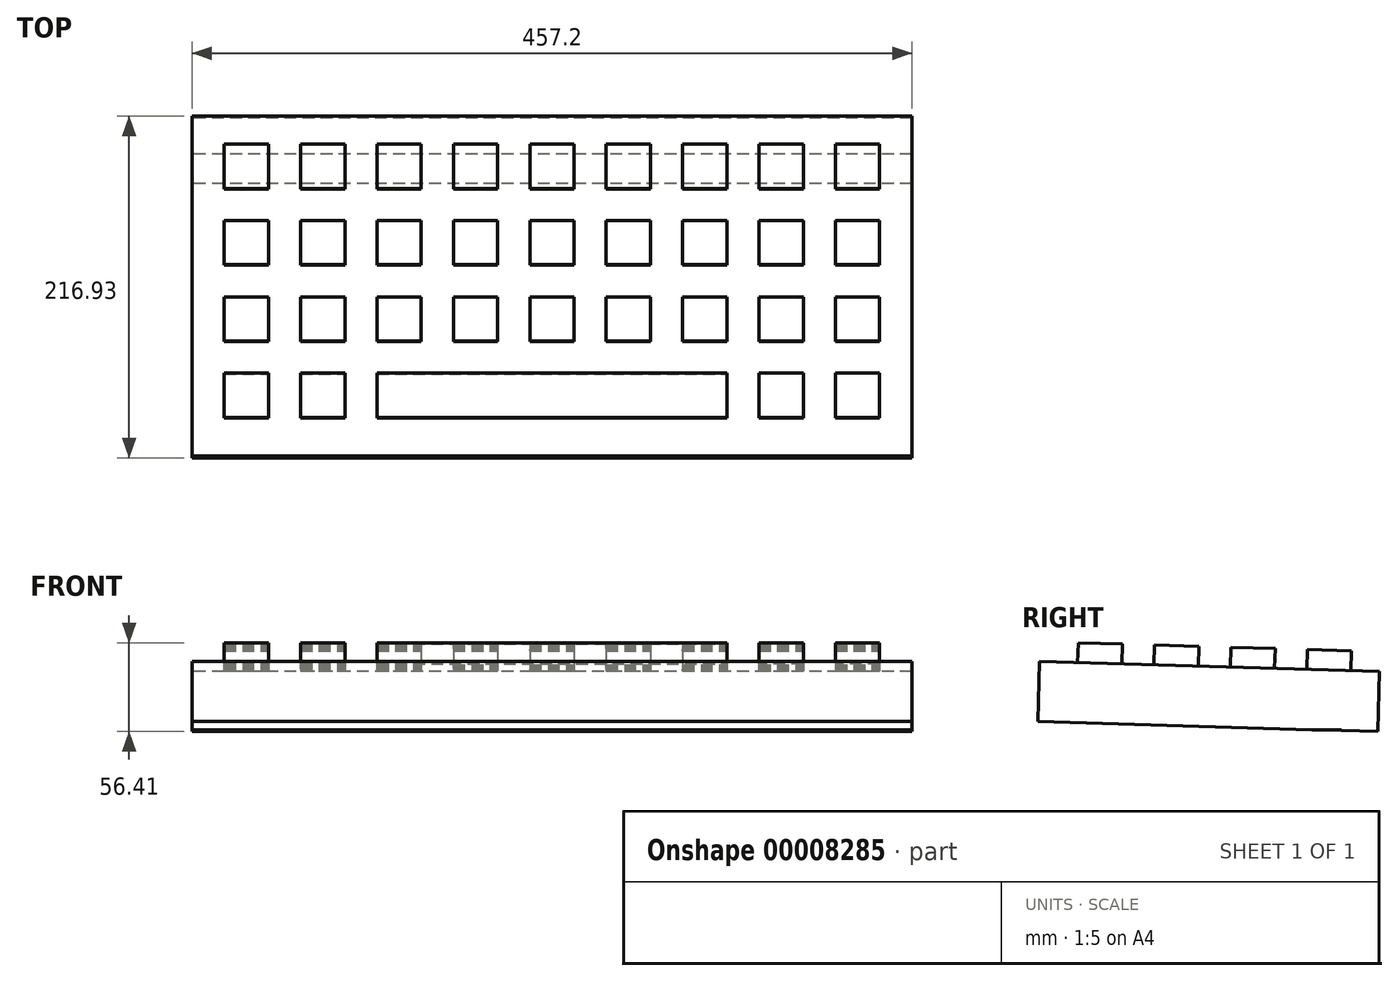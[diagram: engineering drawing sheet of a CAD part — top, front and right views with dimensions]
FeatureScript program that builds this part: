
annotation { "Feature Type Name" : "Feature", "Feature Type Description" : "" }
export const myFeature = defineFeature(function(context is Context, id is Id, definition is map)
    precondition{}
    {
        {
            var Q0;
            Q0=qCreatedBy(makeId("Right.planeOp"),FACE);
            var sketch = newSketch(context, id + "F0", { "sketchPlane" : qUnion([Q0])});
            skLineSegment(sketch, "E0", {"start": v(-116.93, 65.63) * mm, "end": v(98.88, 59.28) * mm});
            skLineSegment(sketch, "E1", {"start": v(98.88, 59.28) * mm, "end": v(97.76, 21.2) * mm});
            skLineSegment(sketch, "E2", {"start": v(97.76, 21.2) * mm, "end": v(74.83, 21.87) * mm});
            skLineSegment(sketch, "E3", {"start": v(74.83, 22.42) * mm, "end": v(74.83, 21.87) * mm});
            skLineSegment(sketch, "E4", {"start": v(74.83, 22.42) * mm, "end": v(56.1, 22.42) * mm});
            skLineSegment(sketch, "E5", {"start": v(56.1, 22.42) * mm, "end": v(-118.05, 27.54) * mm});
            skLineSegment(sketch, "E6", {"start": v(-118.05, 27.54) * mm, "end": v(-116.93, 65.63) * mm});
            skSolve(sketch);
        }
        {
            var Q0;
            Q0 = qSketchRegion(id + "F0", true);
            extrude(context, id + "F1", {"entities" : qUnion([Q0]), "depth" : 457.2 * mm});
        }
        {
            var Q0;
            Q0=makeQuery(id+"F1.opExtrude","SWEPT_FACE",FACE,{"disambiguationData":[OSD([sQuery(id+"F0.wireOp",EDGE,"E0")])]});
            var sketch = newSketch(context, id + "F2", { "sketchPlane" : qUnion([Q0])});
            skLineSegment(sketch, "E7.bottom", {"start": v(20.45, 79.02) * mm, "end": v(48.53, 79.02) * mm});
            skLineSegment(sketch, "E7.top", {"start": v(20.45, 50.94) * mm, "end": v(48.53, 50.94) * mm});
            skLineSegment(sketch, "E7.left", {"start": v(20.45, 79.02) * mm, "end": v(20.45, 50.94) * mm});
            skLineSegment(sketch, "E7.right", {"start": v(48.53, 79.02) * mm, "end": v(48.53, 50.94) * mm});
            skLineSegment(sketch, "E8.bottom", {"start": v(68.98, 50.94) * mm, "end": v(97.06, 50.94) * mm});
            skLineSegment(sketch, "E8.top", {"start": v(68.98, 79.02) * mm, "end": v(97.06, 79.02) * mm});
            skLineSegment(sketch, "E8.left", {"start": v(68.98, 50.94) * mm, "end": v(68.98, 79.02) * mm});
            skLineSegment(sketch, "E8.right", {"start": v(97.06, 50.94) * mm, "end": v(97.06, 79.02) * mm});
            skLineSegment(sketch, "E9.bottom", {"start": v(117.5, 79.02) * mm, "end": v(145.58, 79.02) * mm});
            skLineSegment(sketch, "E9.top", {"start": v(117.5, 50.94) * mm, "end": v(145.58, 50.94) * mm});
            skLineSegment(sketch, "E9.left", {"start": v(117.5, 79.02) * mm, "end": v(117.5, 50.94) * mm});
            skLineSegment(sketch, "E9.right", {"start": v(145.58, 79.02) * mm, "end": v(145.58, 50.94) * mm});
            skLineSegment(sketch, "E10.bottom", {"start": v(166.03, 50.94) * mm, "end": v(194.11, 50.94) * mm});
            skLineSegment(sketch, "E10.top", {"start": v(166.03, 79.02) * mm, "end": v(194.11, 79.02) * mm});
            skLineSegment(sketch, "E10.left", {"start": v(166.03, 50.94) * mm, "end": v(166.03, 79.02) * mm});
            skLineSegment(sketch, "E10.right", {"start": v(194.11, 50.94) * mm, "end": v(194.11, 79.02) * mm});
            skLineSegment(sketch, "E11.bottom", {"start": v(214.56, 79.02) * mm, "end": v(242.64, 79.02) * mm});
            skLineSegment(sketch, "E11.top", {"start": v(214.56, 50.94) * mm, "end": v(242.64, 50.94) * mm});
            skLineSegment(sketch, "E11.left", {"start": v(214.56, 79.02) * mm, "end": v(214.56, 50.94) * mm});
            skLineSegment(sketch, "E11.right", {"start": v(242.64, 79.02) * mm, "end": v(242.64, 50.94) * mm});
            skLineSegment(sketch, "E12.bottom", {"start": v(263.09, 50.94) * mm, "end": v(291.17, 50.94) * mm});
            skLineSegment(sketch, "E12.top", {"start": v(263.09, 79.02) * mm, "end": v(291.17, 79.02) * mm});
            skLineSegment(sketch, "E12.left", {"start": v(263.09, 50.94) * mm, "end": v(263.09, 79.02) * mm});
            skLineSegment(sketch, "E12.right", {"start": v(291.17, 50.94) * mm, "end": v(291.17, 79.02) * mm});
            skLineSegment(sketch, "E13.bottom", {"start": v(311.62, 79.02) * mm, "end": v(339.7, 79.02) * mm});
            skLineSegment(sketch, "E13.top", {"start": v(311.62, 50.94) * mm, "end": v(339.7, 50.94) * mm});
            skLineSegment(sketch, "E13.left", {"start": v(311.62, 79.02) * mm, "end": v(311.62, 50.94) * mm});
            skLineSegment(sketch, "E13.right", {"start": v(339.7, 79.02) * mm, "end": v(339.7, 50.94) * mm});
            skLineSegment(sketch, "E14.bottom", {"start": v(360.14, 79.02) * mm, "end": v(388.22, 79.02) * mm});
            skLineSegment(sketch, "E14.top", {"start": v(360.14, 50.94) * mm, "end": v(388.22, 50.94) * mm});
            skLineSegment(sketch, "E14.left", {"start": v(360.14, 79.02) * mm, "end": v(360.14, 50.94) * mm});
            skLineSegment(sketch, "E14.right", {"start": v(388.22, 79.02) * mm, "end": v(388.22, 50.94) * mm});
            skLineSegment(sketch, "E15.bottom", {"start": v(408.67, 50.94) * mm, "end": v(436.75, 50.94) * mm});
            skLineSegment(sketch, "E15.top", {"start": v(408.67, 79.02) * mm, "end": v(436.75, 79.02) * mm});
            skLineSegment(sketch, "E15.left", {"start": v(408.67, 50.94) * mm, "end": v(408.67, 79.02) * mm});
            skLineSegment(sketch, "E15.right", {"start": v(436.75, 50.94) * mm, "end": v(436.75, 79.02) * mm});
            skLineSegment(sketch, "E16", {"start": v(20.45, 28.14) * mm, "end": v(0, 28.14) * mm, "construction": true});
            skLineSegment(sketch, "E17", {"start": v(48.53, 40.9) * mm, "end": v(68.98, 40.9) * mm, "construction": true});
            skLineSegment(sketch, "E18", {"start": v(97.06, 27.55) * mm, "end": v(117.5, 27.55) * mm, "construction": true});
            skLineSegment(sketch, "E19", {"start": v(145.58, 38.46) * mm, "end": v(166.03, 38.46) * mm, "construction": true});
            skLineSegment(sketch, "E20", {"start": v(194.11, 40.45) * mm, "end": v(214.56, 40.45) * mm, "construction": true});
            skLineSegment(sketch, "E21", {"start": v(242.64, 44) * mm, "end": v(263.09, 44) * mm, "construction": true});
            skLineSegment(sketch, "E22", {"start": v(291.17, 43.04) * mm, "end": v(311.62, 43.04) * mm, "construction": true});
            skLineSegment(sketch, "E23", {"start": v(339.7, 40.7) * mm, "end": v(360.14, 40.7) * mm, "construction": true});
            skLineSegment(sketch, "E24", {"start": v(388.22, 42.73) * mm, "end": v(408.67, 42.73) * mm, "construction": true});
            skLineSegment(sketch, "E25", {"start": v(436.75, 39.15) * mm, "end": v(457.2, 39.15) * mm, "construction": true});
            skLineSegment(sketch, "E26.bottom", {"start": v(20.45, 30.5) * mm, "end": v(48.53, 30.5) * mm});
            skLineSegment(sketch, "E26.top", {"start": v(20.45, 2.41) * mm, "end": v(48.53, 2.41) * mm});
            skLineSegment(sketch, "E26.left", {"start": v(20.45, 30.5) * mm, "end": v(20.45, 2.41) * mm});
            skLineSegment(sketch, "E26.right", {"start": v(48.53, 30.5) * mm, "end": v(48.53, 2.41) * mm});
            skLineSegment(sketch, "E27", {"start": v(60.43, 50.94) * mm, "end": v(60.43, 30.5) * mm, "construction": true});
            skLineSegment(sketch, "E28.bottom", {"start": v(68.98, 30.5) * mm, "end": v(97.06, 30.5) * mm});
            skLineSegment(sketch, "E28.top", {"start": v(68.98, 2.41) * mm, "end": v(97.06, 2.41) * mm});
            skLineSegment(sketch, "E28.left", {"start": v(68.98, 30.5) * mm, "end": v(68.98, 2.41) * mm});
            skLineSegment(sketch, "E28.right", {"start": v(97.06, 30.5) * mm, "end": v(97.06, 2.41) * mm});
            skLineSegment(sketch, "E29.bottom", {"start": v(117.5, 30.5) * mm, "end": v(145.58, 30.5) * mm});
            skLineSegment(sketch, "E29.top", {"start": v(117.5, 2.41) * mm, "end": v(145.58, 2.41) * mm});
            skLineSegment(sketch, "E29.left", {"start": v(117.5, 30.5) * mm, "end": v(117.5, 2.41) * mm});
            skLineSegment(sketch, "E29.right", {"start": v(145.58, 30.5) * mm, "end": v(145.58, 2.41) * mm});
            skLineSegment(sketch, "E30.bottom", {"start": v(166.03, 30.5) * mm, "end": v(194.11, 30.5) * mm});
            skLineSegment(sketch, "E30.top", {"start": v(166.03, 2.41) * mm, "end": v(194.11, 2.41) * mm});
            skLineSegment(sketch, "E30.left", {"start": v(166.03, 30.5) * mm, "end": v(166.03, 2.41) * mm});
            skLineSegment(sketch, "E30.right", {"start": v(194.11, 30.5) * mm, "end": v(194.11, 2.41) * mm});
            skLineSegment(sketch, "E31.bottom", {"start": v(214.56, 2.41) * mm, "end": v(242.64, 2.41) * mm});
            skLineSegment(sketch, "E31.top", {"start": v(214.56, 30.5) * mm, "end": v(242.64, 30.5) * mm});
            skLineSegment(sketch, "E31.left", {"start": v(214.56, 2.41) * mm, "end": v(214.56, 30.5) * mm});
            skLineSegment(sketch, "E31.right", {"start": v(242.64, 2.41) * mm, "end": v(242.64, 30.5) * mm});
            skLineSegment(sketch, "E32.bottom", {"start": v(263.09, 30.5) * mm, "end": v(291.17, 30.5) * mm});
            skLineSegment(sketch, "E32.top", {"start": v(263.09, 2.41) * mm, "end": v(291.17, 2.41) * mm});
            skLineSegment(sketch, "E32.left", {"start": v(263.09, 30.5) * mm, "end": v(263.09, 2.41) * mm});
            skLineSegment(sketch, "E32.right", {"start": v(291.17, 30.5) * mm, "end": v(291.17, 2.41) * mm});
            skLineSegment(sketch, "E33.bottom", {"start": v(311.62, 2.41) * mm, "end": v(339.7, 2.41) * mm});
            skLineSegment(sketch, "E33.top", {"start": v(311.62, 30.5) * mm, "end": v(339.7, 30.5) * mm});
            skLineSegment(sketch, "E33.left", {"start": v(311.62, 2.41) * mm, "end": v(311.62, 30.5) * mm});
            skLineSegment(sketch, "E33.right", {"start": v(339.7, 2.41) * mm, "end": v(339.7, 30.5) * mm});
            skLineSegment(sketch, "E34.bottom", {"start": v(360.14, 30.5) * mm, "end": v(388.22, 30.5) * mm});
            skLineSegment(sketch, "E34.top", {"start": v(360.14, 2.41) * mm, "end": v(388.22, 2.41) * mm});
            skLineSegment(sketch, "E34.left", {"start": v(360.14, 30.5) * mm, "end": v(360.14, 2.41) * mm});
            skLineSegment(sketch, "E34.right", {"start": v(388.22, 30.5) * mm, "end": v(388.22, 2.41) * mm});
            skLineSegment(sketch, "E35.bottom", {"start": v(408.67, 2.41) * mm, "end": v(436.75, 2.41) * mm});
            skLineSegment(sketch, "E35.top", {"start": v(408.67, 30.5) * mm, "end": v(436.75, 30.5) * mm});
            skLineSegment(sketch, "E35.left", {"start": v(408.67, 2.41) * mm, "end": v(408.67, 30.5) * mm});
            skLineSegment(sketch, "E35.right", {"start": v(436.75, 2.41) * mm, "end": v(436.75, 30.5) * mm});
            skLineSegment(sketch, "E36", {"start": v(56.4, 2.41) * mm, "end": v(56.4, -18.03) * mm, "construction": true});
            skLineSegment(sketch, "E37.bottom", {"start": v(20.45, -18.03) * mm, "end": v(48.53, -18.03) * mm});
            skLineSegment(sketch, "E37.top", {"start": v(20.45, -46.11) * mm, "end": v(48.53, -46.11) * mm});
            skLineSegment(sketch, "E37.left", {"start": v(20.45, -18.03) * mm, "end": v(20.45, -46.11) * mm});
            skLineSegment(sketch, "E37.right", {"start": v(48.53, -18.03) * mm, "end": v(48.53, -46.11) * mm});
            skLineSegment(sketch, "E38", {"start": v(59.82, -46.11) * mm, "end": v(59.82, -66.56) * mm, "construction": true});
            skLineSegment(sketch, "E39.bottom", {"start": v(20.45, -66.56) * mm, "end": v(48.53, -66.56) * mm});
            skLineSegment(sketch, "E39.top", {"start": v(20.45, -94.64) * mm, "end": v(48.53, -94.64) * mm});
            skLineSegment(sketch, "E39.left", {"start": v(20.45, -66.56) * mm, "end": v(20.45, -94.64) * mm});
            skLineSegment(sketch, "E39.right", {"start": v(48.53, -66.56) * mm, "end": v(48.53, -94.64) * mm});
            skLineSegment(sketch, "E40.bottom", {"start": v(68.98, -18.03) * mm, "end": v(97.06, -18.03) * mm});
            skLineSegment(sketch, "E40.top", {"start": v(68.98, -46.11) * mm, "end": v(97.06, -46.11) * mm});
            skLineSegment(sketch, "E40.left", {"start": v(68.98, -18.03) * mm, "end": v(68.98, -46.11) * mm});
            skLineSegment(sketch, "E40.right", {"start": v(97.06, -18.03) * mm, "end": v(97.06, -46.11) * mm});
            skLineSegment(sketch, "E41.bottom", {"start": v(117.5, -18.03) * mm, "end": v(145.58, -18.03) * mm});
            skLineSegment(sketch, "E41.top", {"start": v(117.5, -46.11) * mm, "end": v(145.58, -46.11) * mm});
            skLineSegment(sketch, "E41.left", {"start": v(117.5, -18.03) * mm, "end": v(117.5, -46.11) * mm});
            skLineSegment(sketch, "E41.right", {"start": v(145.58, -18.03) * mm, "end": v(145.58, -46.11) * mm});
            skLineSegment(sketch, "E42.bottom", {"start": v(166.03, -18.03) * mm, "end": v(194.11, -18.03) * mm});
            skLineSegment(sketch, "E42.top", {"start": v(166.03, -46.11) * mm, "end": v(194.11, -46.11) * mm});
            skLineSegment(sketch, "E42.left", {"start": v(166.03, -18.03) * mm, "end": v(166.03, -46.11) * mm});
            skLineSegment(sketch, "E42.right", {"start": v(194.11, -18.03) * mm, "end": v(194.11, -46.11) * mm});
            skLineSegment(sketch, "E43.bottom", {"start": v(214.56, -46.11) * mm, "end": v(242.64, -46.11) * mm});
            skLineSegment(sketch, "E43.top", {"start": v(214.56, -18.03) * mm, "end": v(242.64, -18.03) * mm});
            skLineSegment(sketch, "E43.left", {"start": v(214.56, -46.11) * mm, "end": v(214.56, -18.03) * mm});
            skLineSegment(sketch, "E43.right", {"start": v(242.64, -46.11) * mm, "end": v(242.64, -18.03) * mm});
            skLineSegment(sketch, "E44.bottom", {"start": v(263.09, -18.03) * mm, "end": v(291.17, -18.03) * mm});
            skLineSegment(sketch, "E44.top", {"start": v(263.09, -46.11) * mm, "end": v(291.17, -46.11) * mm});
            skLineSegment(sketch, "E44.left", {"start": v(263.09, -18.03) * mm, "end": v(263.09, -46.11) * mm});
            skLineSegment(sketch, "E44.right", {"start": v(291.17, -18.03) * mm, "end": v(291.17, -46.11) * mm});
            skLineSegment(sketch, "E45.bottom", {"start": v(311.62, -46.11) * mm, "end": v(339.7, -46.11) * mm});
            skLineSegment(sketch, "E45.top", {"start": v(311.62, -18.03) * mm, "end": v(339.7, -18.03) * mm});
            skLineSegment(sketch, "E45.left", {"start": v(311.62, -46.11) * mm, "end": v(311.62, -18.03) * mm});
            skLineSegment(sketch, "E45.right", {"start": v(339.7, -46.11) * mm, "end": v(339.7, -18.03) * mm});
            skLineSegment(sketch, "E46.bottom", {"start": v(360.14, -18.03) * mm, "end": v(388.22, -18.03) * mm});
            skLineSegment(sketch, "E46.top", {"start": v(360.14, -46.11) * mm, "end": v(388.22, -46.11) * mm});
            skLineSegment(sketch, "E46.left", {"start": v(360.14, -18.03) * mm, "end": v(360.14, -46.11) * mm});
            skLineSegment(sketch, "E46.right", {"start": v(388.22, -18.03) * mm, "end": v(388.22, -46.11) * mm});
            skLineSegment(sketch, "E47.bottom", {"start": v(408.67, -46.11) * mm, "end": v(436.75, -46.11) * mm});
            skLineSegment(sketch, "E47.top", {"start": v(408.67, -18.03) * mm, "end": v(436.75, -18.03) * mm});
            skLineSegment(sketch, "E47.left", {"start": v(408.67, -46.11) * mm, "end": v(408.67, -18.03) * mm});
            skLineSegment(sketch, "E47.right", {"start": v(436.75, -46.11) * mm, "end": v(436.75, -18.03) * mm});
            skLineSegment(sketch, "E48.bottom", {"start": v(436.75, -94.64) * mm, "end": v(408.67, -94.64) * mm});
            skLineSegment(sketch, "E48.top", {"start": v(436.75, -66.56) * mm, "end": v(408.67, -66.56) * mm});
            skLineSegment(sketch, "E48.left", {"start": v(436.75, -94.64) * mm, "end": v(436.75, -66.56) * mm});
            skLineSegment(sketch, "E48.right", {"start": v(408.67, -94.64) * mm, "end": v(408.67, -66.56) * mm});
            skLineSegment(sketch, "E49.bottom", {"start": v(388.22, -66.56) * mm, "end": v(360.14, -66.56) * mm});
            skLineSegment(sketch, "E49.top", {"start": v(388.22, -94.64) * mm, "end": v(360.14, -94.64) * mm});
            skLineSegment(sketch, "E49.left", {"start": v(388.22, -66.56) * mm, "end": v(388.22, -94.64) * mm});
            skLineSegment(sketch, "E49.right", {"start": v(360.14, -66.56) * mm, "end": v(360.14, -94.64) * mm});
            skLineSegment(sketch, "E50.bottom", {"start": v(68.98, -66.56) * mm, "end": v(97.06, -66.56) * mm});
            skLineSegment(sketch, "E50.top", {"start": v(68.98, -94.64) * mm, "end": v(97.06, -94.64) * mm});
            skLineSegment(sketch, "E50.left", {"start": v(68.98, -66.56) * mm, "end": v(68.98, -94.64) * mm});
            skLineSegment(sketch, "E50.right", {"start": v(97.06, -66.56) * mm, "end": v(97.06, -94.64) * mm});
            skLineSegment(sketch, "E51.bottom", {"start": v(117.5, -66.56) * mm, "end": v(339.7, -66.56) * mm});
            skLineSegment(sketch, "E51.top", {"start": v(117.5, -94.64) * mm, "end": v(339.7, -94.64) * mm});
            skLineSegment(sketch, "E51.left", {"start": v(117.5, -66.56) * mm, "end": v(117.5, -94.64) * mm});
            skLineSegment(sketch, "E51.right", {"start": v(339.7, -66.56) * mm, "end": v(339.7, -94.64) * mm});
            skSolve(sketch);
        }
        {
            var Q0;
            Q0 = qSketchRegion(id + "F2", true);
            extrude(context, id + "F3", {"entities" : qUnion([Q0]), "operationType" : NewBodyOperationType.ADD, "depth" : 12.7 * mm});
        }
    });
